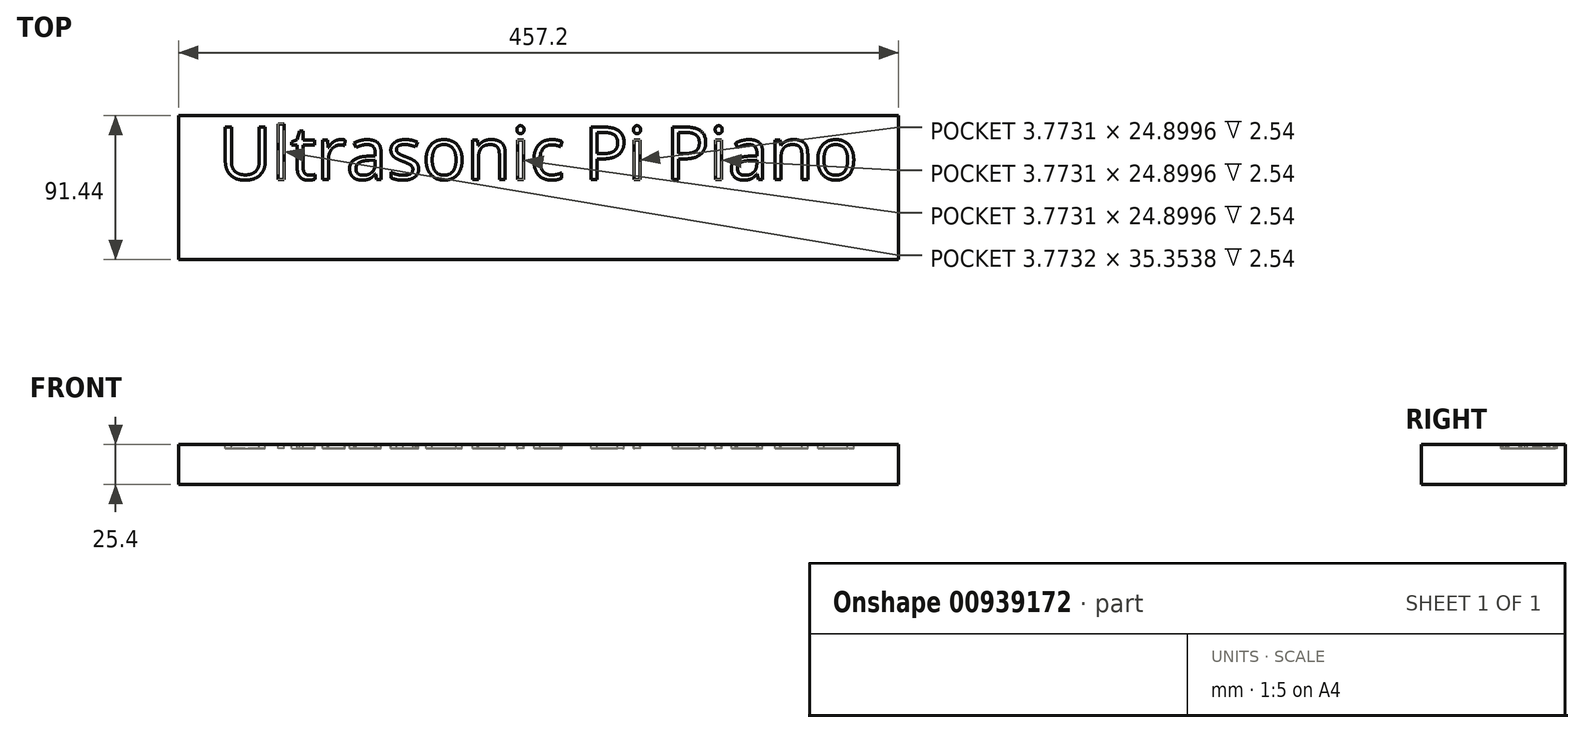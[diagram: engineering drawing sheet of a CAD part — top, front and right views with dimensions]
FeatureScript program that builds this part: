
annotation { "Feature Type Name" : "Feature", "Feature Type Description" : "" }
export const myFeature = defineFeature(function(context is Context, id is Id, definition is map)
    precondition{}
    {
        {
            var Q0;
            Q0=qCreatedBy(makeId("Top.planeOp"),FACE);
            var sketch = newSketch(context, id + "F0", { "sketchPlane" : qUnion([Q0])});
            skLineSegment(sketch, "E0.bottom", {"start": v(0, -127) * mm, "end": v(-457.2, -127) * mm});
            skLineSegment(sketch, "E0.top", {"start": v(0, -218.44) * mm, "end": v(-457.2, -218.44) * mm});
            skLineSegment(sketch, "E0.left", {"start": v(0, -127) * mm, "end": v(0, -218.44) * mm});
            skLineSegment(sketch, "E0.right", {"start": v(-457.2, -127) * mm, "end": v(-457.2, -218.44) * mm});
            skSolve(sketch);
        }
        {
            var Q0;
            Q0=makeQuery(id+"F0.imprint","IMPRINT",FACE,{"disambiguationData":[TD([[makeQuery(id+"F0.imprint","IMPRINT",EDGE,{"derivedFrom":sQuery(id+"F0.wireOp",EDGE,"E0.bottom")}),1.0]])]});
            extrude(context, id + "F1", {"entities" : qUnion([Q0]), "depth" : 25.4 * mm, "offsetDistance" : 25.4 * mm});
        }
        {
            var Q0;
            Q0=makeQuery(id+"F1.opExtrude","CAP_FACE",FACE,{"disambiguationData":[OSD([sQuery(id+"F0.wireOp",EDGE,"E0.bottom"),sQuery(id+"F0.wireOp",EDGE,"E0.top"),sQuery(id+"F0.wireOp",EDGE,"E0.left"),sQuery(id+"F0.wireOp",EDGE,"E0.right")])],"isStart":false});
            var sketch = newSketch(context, id + "F2", { "sketchPlane" : qUnion([Q0])});
            skText(sketch, "E1", { "text": "Ultrasonic Pi Piano", "fontName": "OpenSans-Regular.ttf"});
            const initialGuessF2  = {"E1": [-0.4318, -0.16764, 1, 0, 0.0335]};
            skSetInitialGuess(sketch, initialGuessF2);
            skSolve(sketch);
        }
        {
            var Q0;
            Q0 = qSketchRegion(id + "F2", true);
            extrude(context, id + "F3", {"entities" : qUnion([Q0]), "operationType" : NewBodyOperationType.REMOVE, "oppositeDirection" : true, "depth" : 2.54 * mm, "offsetDistance" : 25.4 * mm});
        }
    });
